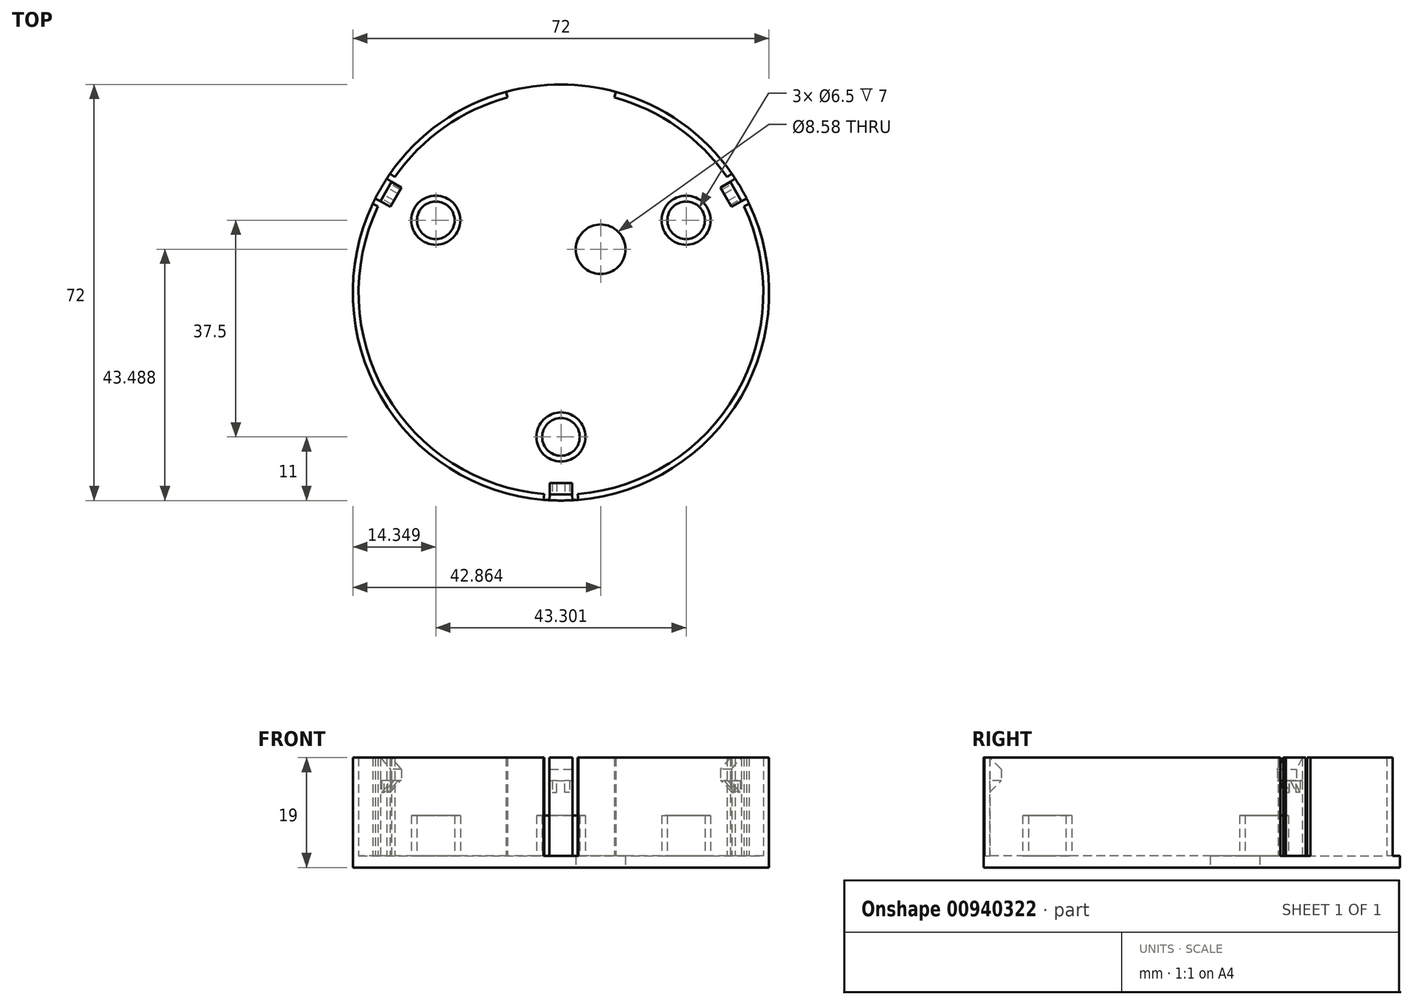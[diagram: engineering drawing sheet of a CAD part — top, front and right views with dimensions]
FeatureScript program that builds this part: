
annotation { "Feature Type Name" : "Feature", "Feature Type Description" : "" }
export const myFeature = defineFeature(function(context is Context, id is Id, definition is map)
    precondition{}
    {
        {
            var Q0;
            Q0=qCreatedBy(makeId("Top.planeOp"),FACE);
            var sketch = newSketch(context, id + "F0", { "sketchPlane" : qUnion([Q0])});
            skLineSegment(sketch, "E0", {"start": v(-12.08, -10.65) * mm, "end": v(-20, 29.41) * mm});
            skLineSegment(sketch, "E1", {"start": v(-20, 29.41) * mm, "end": v(-13.23, 28.16) * mm});
            skLineSegment(sketch, "E2", {"start": v(-13.94, -1.22) * mm, "end": v(-20.89, 17.48) * mm});
            skLineSegment(sketch, "E3", {"start": v(-20.89, 17.48) * mm, "end": v(-24.36, 20.86) * mm});
            skLineSegment(sketch, "E4", {"start": v(-24.36, 20.86) * mm, "end": v(-22.06, 20.86) * mm});
            skLineSegment(sketch, "E5", {"start": v(-22.06, 20.86) * mm, "end": v(-23.65, 24.84) * mm});
            skLineSegment(sketch, "E6", {"start": v(-23.65, 24.84) * mm, "end": v(-19.1, 24.84) * mm});
            skArc(sketch, "E7", {"start": v(0, 30.53) * mm, "mid": v(-6.72, 29.92) * mm, "end": v(-13.23, 28.16) * mm});
            skLineSegment(sketch, "E8", {"start": v(-13.05, -5.72) * mm, "end": v(-23.6, -5.72) * mm});
            skLineSegment(sketch, "E9", {"start": v(-23.6, -5.72) * mm, "end": v(-6.75, -24.12) * mm});
            skLineSegment(sketch, "E10", {"start": v(-6.7, -21.63) * mm, "end": v(0, -29.95) * mm});
            skLineSegment(sketch, "E11", {"start": v(-6.75, -24.12) * mm, "end": v(-3.8, -25.24) * mm});
            skLineSegment(sketch, "E12", {"start": v(0, 30.53) * mm, "end": v(0, 0) * mm, "construction": true});
            skLineSegment(sketch, "E13", {"start": v(0, 0) * mm, "end": v(0, -29.95) * mm, "construction": true});
            skLineSegment(sketch, "E14", {"start": v(-12.08, -10.65) * mm, "end": v(0, -25) * mm});
            skLineSegment(sketch, "E15", {"start": v(-6.7, -21.63) * mm, "end": v(-9.49, -13.73) * mm});
            skLineSegment(sketch, "E16.MirrorCS", {"start": v(24.36, 20.86) * mm, "end": v(22.06, 20.86) * mm});
            skLineSegment(sketch, "E17.MirrorCS", {"start": v(13.05, -5.72) * mm, "end": v(23.6, -5.72) * mm});
            skLineSegment(sketch, "E18.MirrorCS", {"start": v(12.08, -10.65) * mm, "end": v(20, 29.41) * mm});
            skLineSegment(sketch, "E19.MirrorCS", {"start": v(13.94, -1.22) * mm, "end": v(20.89, 17.48) * mm});
            skLineSegment(sketch, "E20.MirrorCS", {"start": v(6.7, -21.63) * mm, "end": v(0, -29.95) * mm});
            skLineSegment(sketch, "E21.MirrorCS", {"start": v(20.89, 17.48) * mm, "end": v(24.36, 20.86) * mm});
            skLineSegment(sketch, "E22.MirrorCS", {"start": v(6.7, -21.63) * mm, "end": v(9.49, -13.73) * mm});
            skLineSegment(sketch, "E23.MirrorCS", {"start": v(20, 29.41) * mm, "end": v(13.23, 28.16) * mm});
            skLineSegment(sketch, "E24.MirrorCS", {"start": v(22.06, 20.86) * mm, "end": v(23.65, 24.84) * mm});
            skLineSegment(sketch, "E25.MirrorCS", {"start": v(23.6, -5.72) * mm, "end": v(6.75, -24.12) * mm});
            skLineSegment(sketch, "E26.MirrorCS", {"start": v(6.75, -24.12) * mm, "end": v(3.8, -25.24) * mm});
            skLineSegment(sketch, "E27.MirrorCS", {"start": v(23.65, 24.84) * mm, "end": v(19.1, 24.84) * mm});
            skLineSegment(sketch, "E28.MirrorCS", {"start": v(12.08, -10.65) * mm, "end": v(0, -25) * mm});
            skArc(sketch, "E29.MirrorCS", {"start": v(0, 30.53) * mm, "mid": v(6.72, 29.92) * mm, "end": v(13.23, 28.16) * mm});
            skCircle(sketch, "E30", {"center": v(-6.86, 10.49) * mm, "radius": 4.29 * mm});
            skCircle(sketch, "E31", {"center": v(0, 21.62) * mm, "radius": 2.38 * mm});
            skCircle(sketch, "E32.MirrorC", {"center": v(6.86, 10.49) * mm, "radius": 4.29 * mm});
            skLineSegment(sketch, "E33", {"start": v(0, -29.95) * mm, "end": v(0, -32.75) * mm, "construction": true});
            skPoint(sketch, "E34.center", {"position": v(0, 3) * mm});
            skCircle(sketch, "E35", {"center": v(0, 3) * mm, "radius": 36 * mm});
            skSolve(sketch);
        }
        {
            var Q0;
            {var subQ0=sQuery(id+"F0.wireOp",EDGE,"E2");Q0=makeQuery(id+"F0.imprint","IMPRINT",FACE,{"disambiguationData":[TD([[makeQuery(id+"F0.imprint","IMPRINT",EDGE,{"derivedFrom":subQ0}),1.0]])]});}
            var Q1;
            {var subQ5=sQuery(id+"F0.wireOp",EDGE,"E17.MirrorCS");Q1=makeQuery(id+"F0.imprint","IMPRINT",FACE,{"disambiguationData":[TD([[makeQuery(id+"F0.imprint","IMPRINT",EDGE,{"derivedFrom":subQ5}),1.0]])]});}
            var Q2;
            Q2=makeQuery(id+"F0.imprint","IMPRINT",FACE,{"disambiguationData":[TD([[makeQuery(id+"F0.imprint","IMPRINT",EDGE,{"derivedFrom":sQuery(id+"F0.wireOp",EDGE,"E16.MirrorCS")}),-1.0]])]});
            var Q3;
            {var subQ0=sQuery(id+"F0.wireOp",EDGE,"E1");Q3=makeQuery(id+"F0.imprint","IMPRINT",FACE,{"disambiguationData":[TD([[makeQuery(id+"F0.imprint","IMPRINT",EDGE,{"derivedFrom":subQ0}),1.0]])]});}
            var Q4;
            Q4=makeQuery(id+"F0.imprint","IMPRINT",FACE,{"disambiguationData":[TD([[makeQuery(id+"F0.imprint","IMPRINT",EDGE,{"derivedFrom":sQuery(id+"F0.wireOp",EDGE,"E31")}),1.0]])]});
            var Q5;
            {var subQ3=sQuery(id+"F0.wireOp",EDGE,"E8");Q5=makeQuery(id+"F0.imprint","IMPRINT",FACE,{"disambiguationData":[TD([[makeQuery(id+"F0.imprint","IMPRINT",EDGE,{"derivedFrom":subQ3}),1.0]])]});}
            var Q6;
            {var subQ3=sQuery(id+"F0.wireOp",EDGE,"E15");Q6=makeQuery(id+"F0.imprint","IMPRINT",FACE,{"disambiguationData":[TD([[makeQuery(id+"F0.imprint","IMPRINT",EDGE,{"derivedFrom":subQ3}),-1.0]])]});}
            var Q7;
            {var subQ4=sQuery(id+"F0.wireOp",EDGE,"E17.MirrorCS");Q7=makeQuery(id+"F0.imprint","IMPRINT",FACE,{"disambiguationData":[TD([[makeQuery(id+"F0.imprint","IMPRINT",EDGE,{"derivedFrom":subQ4}),-1.0]])]});}
            var Q8;
            {var subQ9=sQuery(id+"F0.wireOp",EDGE,"E1");Q8=makeQuery(id+"F0.imprint","IMPRINT",FACE,{"disambiguationData":[TD([[makeQuery(id+"F0.imprint","IMPRINT",EDGE,{"derivedFrom":subQ9}),-1.0]])]});}
            var Q9;
            Q9=makeQuery(id+"F0.imprint","IMPRINT",FACE,{"disambiguationData":[TD([[makeQuery(id+"F0.imprint","IMPRINT",EDGE,{"derivedFrom":sQuery(id+"F0.wireOp",EDGE,"E16.MirrorCS")}),1.0]])]});
            var Q10;
            {var subQ0=sQuery(id+"F0.wireOp",EDGE,"E2");Q10=makeQuery(id+"F0.imprint","IMPRINT",FACE,{"disambiguationData":[TD([[makeQuery(id+"F0.imprint","IMPRINT",EDGE,{"derivedFrom":subQ0}),-1.0]])]});}
            var Q11;
            Q11=makeQuery(id+"F0.imprint","IMPRINT",FACE,{"disambiguationData":[TD([[makeQuery(id+"F0.imprint","IMPRINT",EDGE,{"derivedFrom":sQuery(id+"F0.wireOp",EDGE,"E32.MirrorC")}),-1.0]])]});
            var Q12;
            Q12=makeQuery(id+"F0.imprint","IMPRINT",FACE,{"disambiguationData":[TD([[makeQuery(id+"F0.imprint","IMPRINT",EDGE,{"derivedFrom":sQuery(id+"F0.wireOp",EDGE,"E30")}),1.0]])]});
            var Q13;
            {var subQ0=sQuery(id+"F0.wireOp",EDGE,"TDbvBT22-fM1V-MBm7-Nu63-0sPaSuEuKLQy");Q13=makeQuery(id+"F0.imprint","IMPRINT",FACE,{"disambiguationData":[TD([[makeQuery(id+"F0.imprint","IMPRINT",EDGE,{"derivedFrom":subQ0}),-1.0]])]});}
            extrude(context, id + "F1", {"entities" : qUnion([Q0, Q1, Q2, Q3, Q4, Q5, Q6, Q7, Q8, Q9, Q10, Q11, Q12, Q13]), "depth" : 2 * mm, "offsetDistance" : 25 * mm});
        }
        {
            var Q0;
            Q0=makeQuery(id+"F1.opExtrude","CAP_FACE",FACE,{"disambiguationData":[OSD([sQuery(id+"F0.wireOp",EDGE,"E35")])],"isStart":false});
            var sketch = newSketch(context, id + "F2", { "sketchPlane" : qUnion([Q0])});
            skArc(sketch, "E36", {"start": v(1.9, -31.95) * mm, "mid": v(0, 38) * mm, "end": v(-1.9, -31.95) * mm});
            skLineSegment(sketch, "E37", {"start": v(-9.5, 37.72) * mm, "end": v(9.5, 37.72) * mm, "construction": true});
            skLineSegment(sketch, "E38", {"start": v(-9.5, 37.72) * mm, "end": v(-8, 32.21) * mm});
            skLineSegment(sketch, "E39", {"start": v(-9.5, 37.72) * mm, "end": v(3.37, 41.25) * mm, "construction": true});
            skLineSegment(sketch, "E40.MirrorCS", {"start": v(9.5, 37.72) * mm, "end": v(8, 32.21) * mm});
            skCircle(sketch, "E41", {"center": v(0, 3) * mm, "radius": 25 * mm, "construction": true});
            skLineSegment(sketch, "E42", {"start": v(0, 3) * mm, "end": v(0, -33) * mm, "construction": true});
            skCircle(sketch, "E43", {"center": v(0, -22) * mm, "radius": 3.25 * mm});
            skCircle(sketch, "E44", {"center": v(0, -22) * mm, "radius": 4.25 * mm});
            skLineSegment(sketch, "E45", {"start": v(-9.7, -32.32) * mm, "end": v(0, -33.12) * mm, "construction": true});
            skLineSegment(sketch, "E46", {"start": v(-2.99, -32.88) * mm, "end": v(-2.53, -27.37) * mm});
            skLineSegment(sketch, "E47", {"start": v(-2, -32.96) * mm, "end": v(-1.55, -27.67) * mm});
            skLineSegment(sketch, "E48", {"start": v(0, -33) * mm, "end": v(0, -38.95) * mm, "construction": true});
            skLineSegment(sketch, "E49.MirrorCS", {"start": v(2, -32.96) * mm, "end": v(1.55, -27.67) * mm});
            skLineSegment(sketch, "E50.MirrorCS", {"start": v(2.99, -32.88) * mm, "end": v(2.53, -27.37) * mm});
            skLineSegment(sketch, "E51.1.0", {"start": v(32.56, 18.35) * mm, "end": v(27.57, 16) * mm});
            skLineSegment(sketch, "E51.1.1", {"start": v(32.14, 19.25) * mm, "end": v(27.34, 17) * mm});
            skLineSegment(sketch, "E51.1.2", {"start": v(30.14, 22.7) * mm, "end": v(25.79, 19.68) * mm});
            skLineSegment(sketch, "E51.1.3", {"start": v(29.57, 23.53) * mm, "end": v(25.04, 20.38) * mm});
            skLineSegment(sketch, "E51.2.0", {"start": v(-29.57, 23.53) * mm, "end": v(-25.04, 20.38) * mm});
            skLineSegment(sketch, "E51.2.1", {"start": v(-30.14, 22.7) * mm, "end": v(-25.79, 19.68) * mm});
            skLineSegment(sketch, "E51.2.2", {"start": v(-32.14, 19.25) * mm, "end": v(-27.34, 17) * mm});
            skLineSegment(sketch, "E51.2.3", {"start": v(-32.56, 18.35) * mm, "end": v(-27.57, 16) * mm});
            skLineSegment(sketch, "E52", {"start": v(-1.9, -31.95) * mm, "end": v(1.9, -31.95) * mm});
            skLineSegment(sketch, "E53", {"start": v(0, 3) * mm, "end": v(0, 37.72) * mm, "construction": true});
            skLineSegment(sketch, "E54", {"start": v(-1.53, -31.95) * mm, "end": v(-1.53, -29.95) * mm});
            skLineSegment(sketch, "E55", {"start": v(-1.53, -29.95) * mm, "end": v(-0.73, -29.95) * mm});
            skLineSegment(sketch, "E56", {"start": v(-0.73, -29.95) * mm, "end": v(-0.73, -31.95) * mm});
            skLineSegment(sketch, "E57", {"start": v(1.38, -31.95) * mm, "end": v(1.38, -29.95) * mm});
            skLineSegment(sketch, "E58", {"start": v(1.38, -29.95) * mm, "end": v(0.58, -29.95) * mm});
            skLineSegment(sketch, "E59", {"start": v(0.58, -29.95) * mm, "end": v(0.58, -31.95) * mm});
            skSolve(sketch);
        }
        {
            var Q0;
            {var subQ0=sQuery(id+"F2.wireOp",EDGE,"E38");var subQ1=sQuery(id+"F2.wireOp",EDGE,"E36");var subQ2=makeQuery(id+"F2.imprint","INTERSECT",VERTEX,{"derivedFrom":[subQ1,subQ0]});Q0=makeQuery(id+"F2.imprint","IMPRINT",FACE,{"disambiguationData":[TD([[makeQuery(id+"F2.imprint","IMPRINT",EDGE,{"disambiguationData":[TD([[subQ2,-1.0]])],"derivedFrom":subQ1}),-1.0]])]});}
            var Q1;
            {var subQ0=sQuery(id+"F2.wireOp",EDGE,"E51.2.3");var subQ1=sQuery(id+"F2.wireOp",EDGE,"E36");var subQ2=makeQuery(id+"F2.imprint","INTERSECT",VERTEX,{"derivedFrom":[subQ1,subQ0]});Q1=makeQuery(id+"F2.imprint","IMPRINT",FACE,{"disambiguationData":[TD([[makeQuery(id+"F2.imprint","IMPRINT",EDGE,{"disambiguationData":[TD([[subQ2,-1.0]])],"derivedFrom":subQ1}),-1.0]])]});}
            var Q2;
            {var subQ0=sQuery(id+"F2.wireOp",EDGE,"E51.1.0");var subQ1=sQuery(id+"F2.wireOp",EDGE,"E36");var subQ2=makeQuery(id+"F2.imprint","INTERSECT",VERTEX,{"derivedFrom":[subQ1,subQ0]});Q2=makeQuery(id+"F2.imprint","IMPRINT",FACE,{"disambiguationData":[TD([[makeQuery(id+"F2.imprint","IMPRINT",EDGE,{"disambiguationData":[TD([[subQ2,1.0]])],"derivedFrom":subQ1}),-1.0]])]});}
            var Q3;
            {var subQ0=sQuery(id+"F2.wireOp",EDGE,"E51.1.3");var subQ1=sQuery(id+"F2.wireOp",EDGE,"E36");var subQ2=makeQuery(id+"F2.imprint","INTERSECT",VERTEX,{"derivedFrom":[subQ1,subQ0]});Q3=makeQuery(id+"F2.imprint","IMPRINT",FACE,{"disambiguationData":[TD([[makeQuery(id+"F2.imprint","IMPRINT",EDGE,{"disambiguationData":[TD([[subQ2,-1.0]])],"derivedFrom":subQ1}),-1.0]])]});}
            extrude(context, id + "F3", {"entities" : qUnion([Q0, Q1, Q2, Q3]), "operationType" : NewBodyOperationType.ADD, "depth" : 17 * mm, "offsetDistance" : 25 * mm});
        }
        {
            var Q0;
            {var subQ0=sQuery(id+"F2.wireOp",EDGE,"E52");Q0=makeQuery(id+"F2.imprint","IMPRINT",FACE,{"disambiguationData":[TD([[makeQuery(id+"F2.imprint","IMPRINT",EDGE,{"derivedFrom":subQ0}),-1.0]])]});}
            extrude(context, id + "F4", {"entities" : qUnion([Q0]), "depth" : 17 * mm, "offsetDistance" : 25 * mm});
        }
        {
            var Q0;
            Q0=makeQuery(id+"F2.imprint","IMPRINT",FACE,{"disambiguationData":[TD([[makeQuery(id+"F2.imprint","IMPRINT",EDGE,{"derivedFrom":sQuery(id+"F2.wireOp",EDGE,"E43")}),-1.0]])]});
            extrude(context, id + "F5", {"entities" : qUnion([Q0]), "depth" : 7 * mm, "offsetDistance" : 25 * mm});
        }
        {
            var Q0;
            Q0=makeQuery(id+"F5.opExtrude","SWEPT_BODY",BODY,{"disambiguationData":[OSD([sQuery(id+"F2.wireOp",EDGE,"E43"),sQuery(id+"F2.wireOp",EDGE,"E44")])]});
            var Q1;
            Q1=sQuery(id+"F2.wireOp",EDGE,"E41");
            circularPattern(context, id + "F6", {"entities" : qUnion([Q0]), "axis" : qUnion([Q1]), "angle" : 360 * degree, "instanceCount" : 3, "equalSpace" : true});
        }
        {
            var Q0;
            Q0=makeQuery(id+"F4.opExtrude","SWEPT_FACE",FACE,{"disambiguationData":[OSD([sQuery(id+"F2.wireOp",EDGE,"E52")])]});
            var sketch = newSketch(context, id + "F7", { "sketchPlane" : qUnion([Q0])});
            skLineSegment(sketch, "E60.bottom", {"start": v(1.9, 19) * mm, "end": v(-1.9, 19) * mm});
            skLineSegment(sketch, "E60.top", {"start": v(1.9, 15) * mm, "end": v(-1.9, 15) * mm});
            skLineSegment(sketch, "E60.left", {"start": v(1.9, 19) * mm, "end": v(1.9, 15) * mm});
            skLineSegment(sketch, "E60.right", {"start": v(-1.9, 19) * mm, "end": v(-1.9, 15) * mm});
            skLineSegment(sketch, "E61.left", {"start": v(1.9, 15) * mm, "end": v(1.9, 14) * mm});
            skLineSegment(sketch, "E61.right", {"start": v(-1.9, 15) * mm, "end": v(-1.9, 14) * mm});
            skLineSegment(sketch, "E62", {"start": v(-1.47, 15) * mm, "end": v(-1.47, 13) * mm});
            skLineSegment(sketch, "E63", {"start": v(-1.47, 13) * mm, "end": v(-0.67, 13) * mm});
            skLineSegment(sketch, "E64", {"start": v(-0.67, 13) * mm, "end": v(-0.67, 15) * mm});
            skLineSegment(sketch, "E65", {"start": v(1.5, 15) * mm, "end": v(1.5, 13) * mm});
            skLineSegment(sketch, "E66", {"start": v(1.5, 13) * mm, "end": v(0.7, 13) * mm});
            skLineSegment(sketch, "E67", {"start": v(0.7, 13) * mm, "end": v(0.7, 15) * mm});
            skSolve(sketch);
        }
        {
            var Q0;
            Q0=makeQuery(id+"F7.imprint","IMPRINT",FACE,{"disambiguationData":[TD([[makeQuery(id+"F7.imprint","IMPRINT",EDGE,{"derivedFrom":sQuery(id+"F7.wireOp",EDGE,"E60.bottom")}),1.0]])]});
            var Q1;
            {var subQ0=sQuery(id+"F7.wireOp",EDGE,"E62");Q1=makeQuery(id+"F7.imprint","IMPRINT",FACE,{"disambiguationData":[TD([[makeQuery(id+"F7.imprint","IMPRINT",EDGE,{"derivedFrom":subQ0}),1.0]])]});}
            var Q2;
            {var subQ0=sQuery(id+"F7.wireOp",EDGE,"E65");Q2=makeQuery(id+"F7.imprint","IMPRINT",FACE,{"disambiguationData":[TD([[makeQuery(id+"F7.imprint","IMPRINT",EDGE,{"derivedFrom":subQ0}),-1.0]])]});}
            extrude(context, id + "F8", {"entities" : qUnion([Q0, Q1, Q2]), "operationType" : NewBodyOperationType.ADD, "depth" : 2 * mm, "offsetDistance" : 25 * mm});
        }
        {
            var Q0;
            Q0=makeQuery(id+"F8.opExtrude","CAP_EDGE",EDGE,{"disambiguationData":[OSD([sQuery(id+"F7.wireOp",EDGE,"E60.bottom")])],"isStart":false});
            var Q1;
            Q1=makeQuery(id+"F8.opExtrude","CAP_EDGE",EDGE,{"disambiguationData":[OSD([sQuery(id+"F7.wireOp",EDGE,"E61.top")])],"isStart":false});
            var Q2;
            Q2=makeQuery(id+"F8.opExtrude","CAP_EDGE",EDGE,{"disambiguationData":[OSD([sQuery(id+"F7.wireOp",EDGE,"E63")])],"isStart":false});
            var Q3;
            Q3=makeQuery(id+"F8.opExtrude","CAP_EDGE",EDGE,{"disambiguationData":[OSD([sQuery(id+"F7.wireOp",EDGE,"E66")])],"isStart":false});
            chamfer(context, id + "F9", {"entities" : qUnion([Q0, Q1, Q2, Q3]), "width" : 2 * mm, "tangentPropagation" : true});
        }
        {
            var Q0;
            Q0=makeQuery(id+"F4.opExtrude","SWEPT_BODY",BODY,{"disambiguationData":[OSD([sQuery(id+"F0.wireOp",EDGE,"E35"),sQuery(id+"F2.wireOp",EDGE,"E47"),sQuery(id+"F2.wireOp",EDGE,"E49.MirrorCS"),sQuery(id+"F2.wireOp",EDGE,"E52")])]});
            var Q1;
            Q1=sQuery(id+"F2.wireOp",EDGE,"E41");
            circularPattern(context, id + "F10", {"entities" : qUnion([Q0]), "axis" : qUnion([Q1]), "angle" : 360 * degree, "instanceCount" : 3, "equalSpace" : true});
        }
    });
